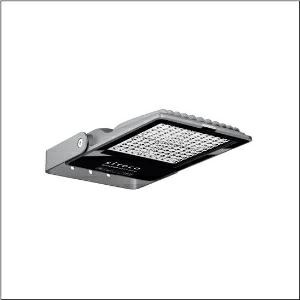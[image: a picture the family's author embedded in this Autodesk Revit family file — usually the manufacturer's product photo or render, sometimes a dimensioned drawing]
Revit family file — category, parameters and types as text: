
# Revit family: sicompact_r__31_mini___pl32_5xa7571f2k23_7a3f
name_source: partatom
category: Lighting Fixtures
units: mm (PartAtom-declared; Revit-internal decimal feet)

## family parameters
Cut with Voids When Loaded = No
Host = Face
Light Source = No
Part Type = Normal
Room Calculation Point = No
Round Connector Dimension = Use Diameter
Shared = No

## types (1)
- SiCompact® 31 mini  PL32 (1 x LED, 20000 lm, 130 W, 4000K)
    Apparent Load = 130 VA
    CIE Flux Codes = 32 69 98 100 100
    Color Rendering = 70
    Color Temperature = 4000K
    Default Elevation = 1800 mm
    Description = SiCompact® 31 mini, floodlight, primary light control with lens, of plastic, of toughened safety glass, transparent, light distribution: PL32, light emission: direct distribution, primary light characteristic: asymmetric, installation type: surface-mounted, LED, High Power LED, rated luminous flux: 20.000lm, luminous efficacy: 154lm/W, light colour: 740, colour temperature: 4000K, control gear: ECG, with cable, 3x 1.5mm², mains connection: 220..240V, AC, 50/60Hz, connection cable pre-assembled, cable length: 2m, rated input power: 130W, of diecast aluminium, specular, metallic grey (RAL 9006), length: 461mm, width: 261mm, height: 62mm, bracket, of sheet steel, coated, metallic grey (RAL 9006), ON/OFF, protection rating (complete): IP66, insulation class (complete): insulation class I (protective earthing), certification: CE, ENEC, impact resistance: IK08, permissible operating ambient temperature: -40..+45°C, packaging unit: 1 piece

Light Distribution: PL32
    Height = 62 mm  [stored 0.203412 ft]
    Lamp = 1 x LED
    Lamp Light Flux = 20000 lm
    Lamp Power = 130 W
    Lamp count = 1
    Length = 460 mm
    Luminous efficacy = 154 lm/W
    Manufacturer = Siteco
    ModVariant = No
    Model = 5XA7571F2K23
    Mounting Place = Wall
    Mounting Type = Surface mounted
    Number of Poles = 1
    OnlyDefault = Yes
    Power Factor = 1
    Product Name = SiCompact® 31 mini | PL32
    Product group = floodlight | wall mounted
    ProductGroupID = 2001
    Protection Class = Protection class I
    Protection Degree = IP 66
    RLX_Detail_Level = 1
    RLX_Emergency_Light_Flux = 0 lm
    RLX_Emergency_Type = 0
    RLX_Emergency_Type_DB = No
    RlxData = <blob elided: 126545 chars, md5=62bba32f>
    Socket = socket
    Standby Power = 0 W
    System Light Flux = 20000 lm
    System Power = 130 W
    Type Comments = Product without accessories
    Type Image = l_1006951.jpg
    URL = http://relux.com
    VarID = ---
    Voltage = 0 V
    Weight = 0.00 kg
    Width = 260 mm

note: [stored X ft] marks values corroborated as IEEE doubles in the binary element streams (Revit-internal decimal feet)

## geometry (parser evidence)
native form markers: Blend x4, Sweep x14
no freeform markers — native parametric forms only
